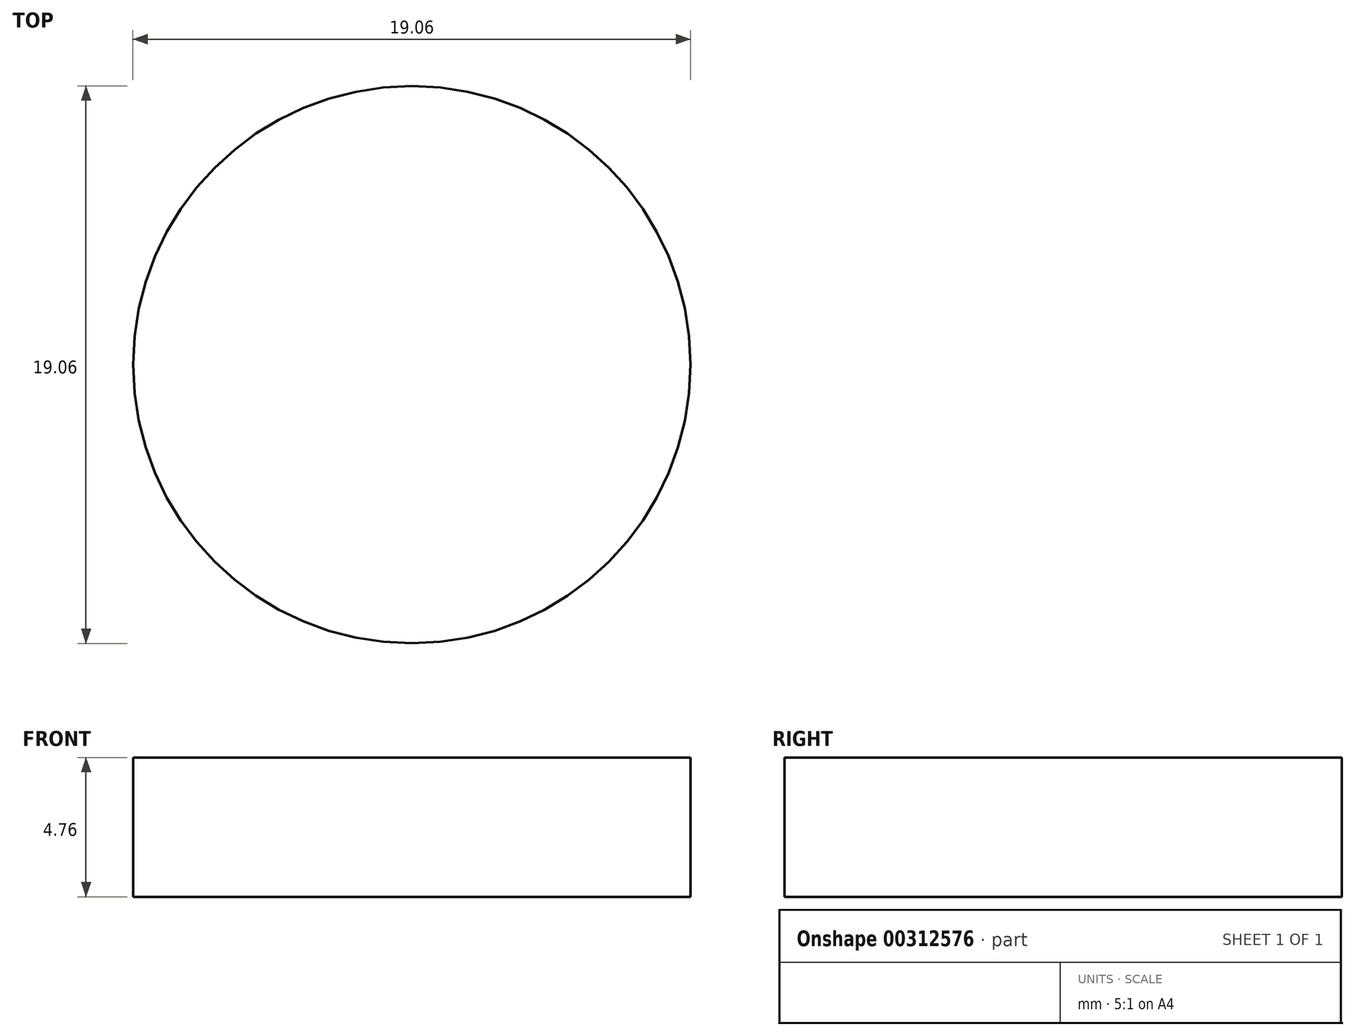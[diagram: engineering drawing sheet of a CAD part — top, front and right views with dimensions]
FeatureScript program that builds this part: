
annotation { "Feature Type Name" : "Feature", "Feature Type Description" : "" }
export const myFeature = defineFeature(function(context is Context, id is Id, definition is map)
    precondition{}
    {
        {
            var Q0;
            Q0=qCreatedBy(makeId("Top.planeOp"),FACE);
            var sketch = newSketch(context, id + "F0", { "sketchPlane" : qUnion([Q0])});
            skCircle(sketch, "E0", {"center": v(0, 0) * mm, "radius": 9.53 * mm});
            skSolve(sketch);
        }
        {
            var Q0;
            Q0=makeQuery(id+"F0.imprint","IMPRINT",FACE,{"disambiguationData":[TD([[makeQuery(id+"F0.imprint","IMPRINT",EDGE,{"derivedFrom":sQuery(id+"F0.wireOp",EDGE,"E0")}),1.0]])]});
            extrude(context, id + "F1", {"entities" : qUnion([Q0]), "depth" : 4.76 * mm});
        }
    });
